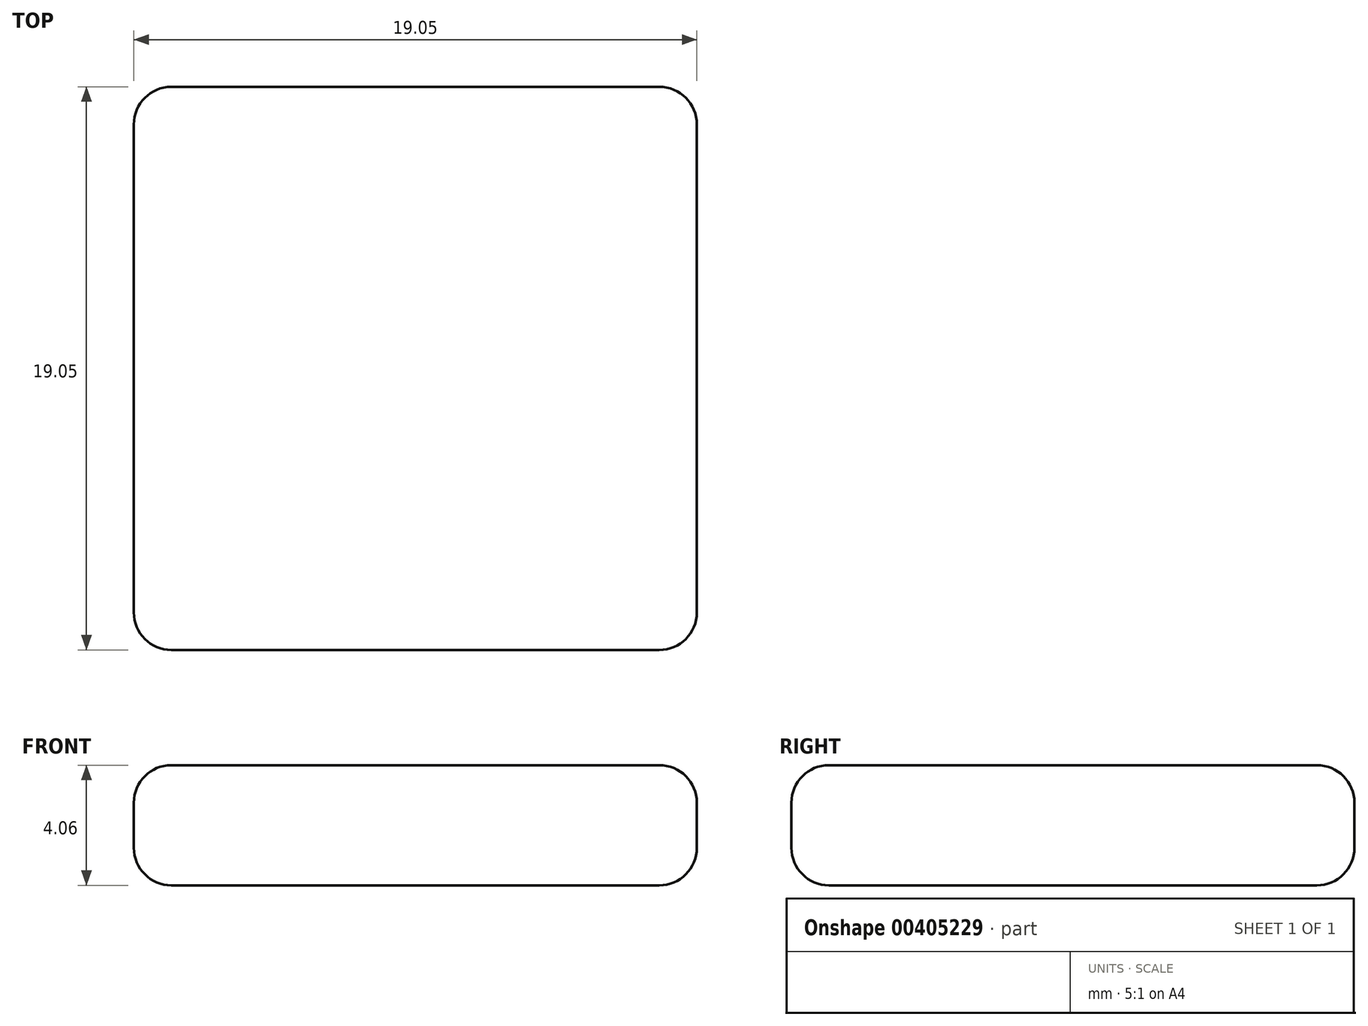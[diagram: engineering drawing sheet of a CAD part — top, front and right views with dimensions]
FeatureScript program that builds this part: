
annotation { "Feature Type Name" : "Feature", "Feature Type Description" : "" }
export const myFeature = defineFeature(function(context is Context, id is Id, definition is map)
    precondition{}
    {
        {
            var Q0;
            Q0=qCreatedBy(makeId("Top.planeOp"),FACE);
            var sketch = newSketch(context, id + "F0", { "sketchPlane" : qUnion([Q0])});
            skLineSegment(sketch, "E0.bottom", {"start": v(0, 0) * mm, "end": v(19.05, 0) * mm});
            skLineSegment(sketch, "E0.top", {"start": v(0, 19.05) * mm, "end": v(19.05, 19.05) * mm});
            skLineSegment(sketch, "E0.left", {"start": v(0, 0) * mm, "end": v(0, 19.05) * mm});
            skLineSegment(sketch, "E0.right", {"start": v(19.05, 0) * mm, "end": v(19.05, 19.05) * mm});
            skSolve(sketch);
        }
        {
            var Q0;
            Q0=makeQuery(id+"F0.imprint","IMPRINT",FACE,{"disambiguationData":[TD([[makeQuery(id+"F0.imprint","IMPRINT",EDGE,{"derivedFrom":sQuery(id+"F0.wireOp",EDGE,"E0.bottom")}),1.0]])]});
            extrude(context, id + "F1", {"entities" : qUnion([Q0]), "depth" : 4.06 * mm});
        }
        {
            var Q0;
            Q0=makeQuery(id+"F1.opExtrude","SWEPT_EDGE",EDGE,{"disambiguationData":[OSD([sQuery(id+"F0.wireOp",EDGE,"E0.bottom"),sQuery(id+"F0.wireOp",EDGE,"E0.right")])]});
            var Q1;
            Q1=makeQuery(id+"F1.opExtrude","CAP_EDGE",EDGE,{"disambiguationData":[OSD([sQuery(id+"F0.wireOp",EDGE,"E0.right")])],"isStart":false});
            var Q2;
            Q2=makeQuery(id+"F1.opExtrude","CAP_EDGE",EDGE,{"disambiguationData":[OSD([sQuery(id+"F0.wireOp",EDGE,"E0.bottom")])],"isStart":false});
            var Q3;
            Q3=makeQuery(id+"F1.opExtrude","CAP_EDGE",EDGE,{"disambiguationData":[OSD([sQuery(id+"F0.wireOp",EDGE,"E0.right")])],"isStart":true});
            var Q4;
            Q4=makeQuery(id+"F1.opExtrude","CAP_EDGE",EDGE,{"disambiguationData":[OSD([sQuery(id+"F0.wireOp",EDGE,"E0.bottom")])],"isStart":true});
            var Q5;
            Q5=makeQuery(id+"F1.opExtrude","SWEPT_EDGE",EDGE,{"disambiguationData":[OSD([sQuery(id+"F0.wireOp",EDGE,"E0.bottom"),sQuery(id+"F0.wireOp",EDGE,"E0.left")])]});
            var Q6;
            Q6=makeQuery(id+"F1.opExtrude","CAP_EDGE",EDGE,{"disambiguationData":[OSD([sQuery(id+"F0.wireOp",EDGE,"E0.left")])],"isStart":false});
            var Q7;
            Q7=makeQuery(id+"F1.opExtrude","SWEPT_EDGE",EDGE,{"disambiguationData":[OSD([sQuery(id+"F0.wireOp",EDGE,"E0.top"),sQuery(id+"F0.wireOp",EDGE,"E0.right")])]});
            var Q8;
            Q8=makeQuery(id+"F1.opExtrude","CAP_EDGE",EDGE,{"disambiguationData":[OSD([sQuery(id+"F0.wireOp",EDGE,"E0.top")])],"isStart":false});
            var Q9;
            Q9=makeQuery(id+"F1.opExtrude","CAP_EDGE",EDGE,{"disambiguationData":[OSD([sQuery(id+"F0.wireOp",EDGE,"E0.top")])],"isStart":true});
            var Q10;
            Q10=makeQuery(id+"F1.opExtrude","SWEPT_EDGE",EDGE,{"disambiguationData":[OSD([sQuery(id+"F0.wireOp",EDGE,"E0.top"),sQuery(id+"F0.wireOp",EDGE,"E0.left")])]});
            var Q11;
            Q11=makeQuery(id+"F1.opExtrude","CAP_EDGE",EDGE,{"disambiguationData":[OSD([sQuery(id+"F0.wireOp",EDGE,"E0.left")])],"isStart":true});
            fillet(context, id + "F2", {"entities" : qUnion([Q0, Q1, Q2, Q3, Q4, Q5, Q6, Q7, Q8, Q9, Q10, Q11]), "radius" : 1.27 * mm, "tangentPropagation" : true, "allowEdgeOverflow" : false});
        }
    });
